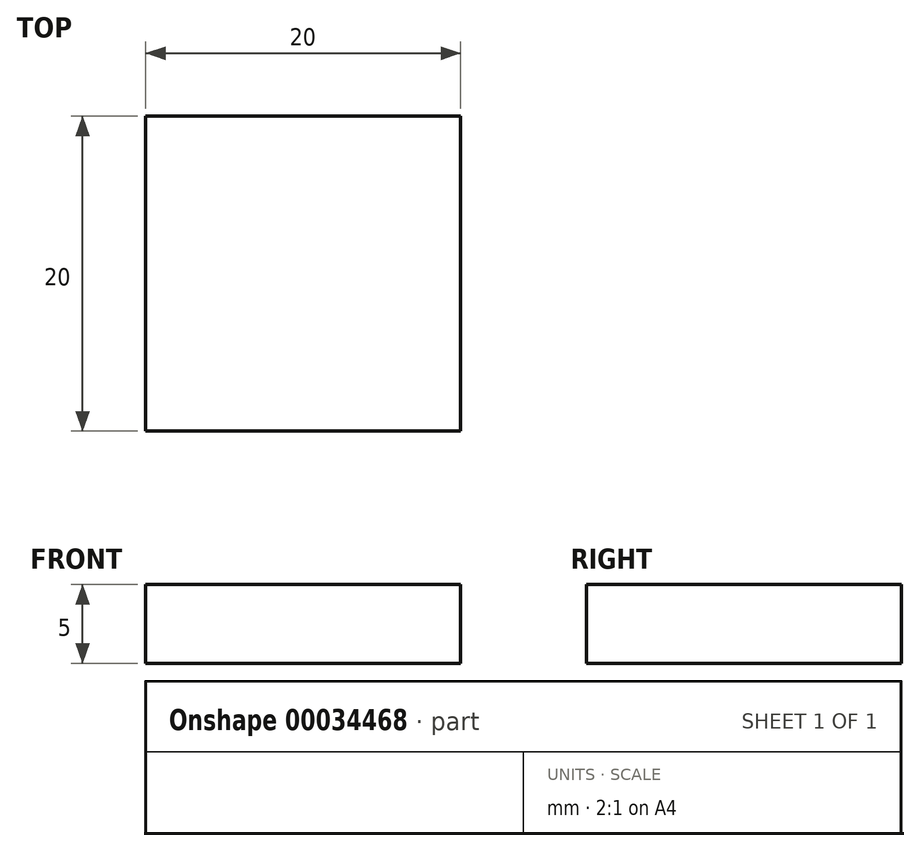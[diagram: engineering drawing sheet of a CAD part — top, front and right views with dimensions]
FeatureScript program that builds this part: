
annotation { "Feature Type Name" : "Feature", "Feature Type Description" : "" }
export const myFeature = defineFeature(function(context is Context, id is Id, definition is map)
    precondition{}
    {
        {
            var Q0;
            Q0=qCreatedBy(makeId("Top.planeOp"),FACE);
            var sketch = newSketch(context, id + "F0", { "sketchPlane" : qUnion([Q0])});
            skLineSegment(sketch, "E0.rect.bottom", {"start": v(10, 10) * mm, "end": v(-10, 10) * mm});
            skLineSegment(sketch, "E0.rect.top", {"start": v(10, -10) * mm, "end": v(-10, -10) * mm});
            skLineSegment(sketch, "E0.rect.left", {"start": v(10, 10) * mm, "end": v(10, -10) * mm});
            skLineSegment(sketch, "E0.rect.right", {"start": v(-10, 10) * mm, "end": v(-10, -10) * mm});
            skPoint(sketch, "E0.rect.middle", {"position": v(0, 0) * mm});
            skSolve(sketch);
        }
        {
            var Q0;
            Q0 = qSketchRegion(id + "F0", true);
            extrude(context, id + "F1", {"entities" : qUnion([Q0]), "depth" : 5 * mm});
        }
    });
